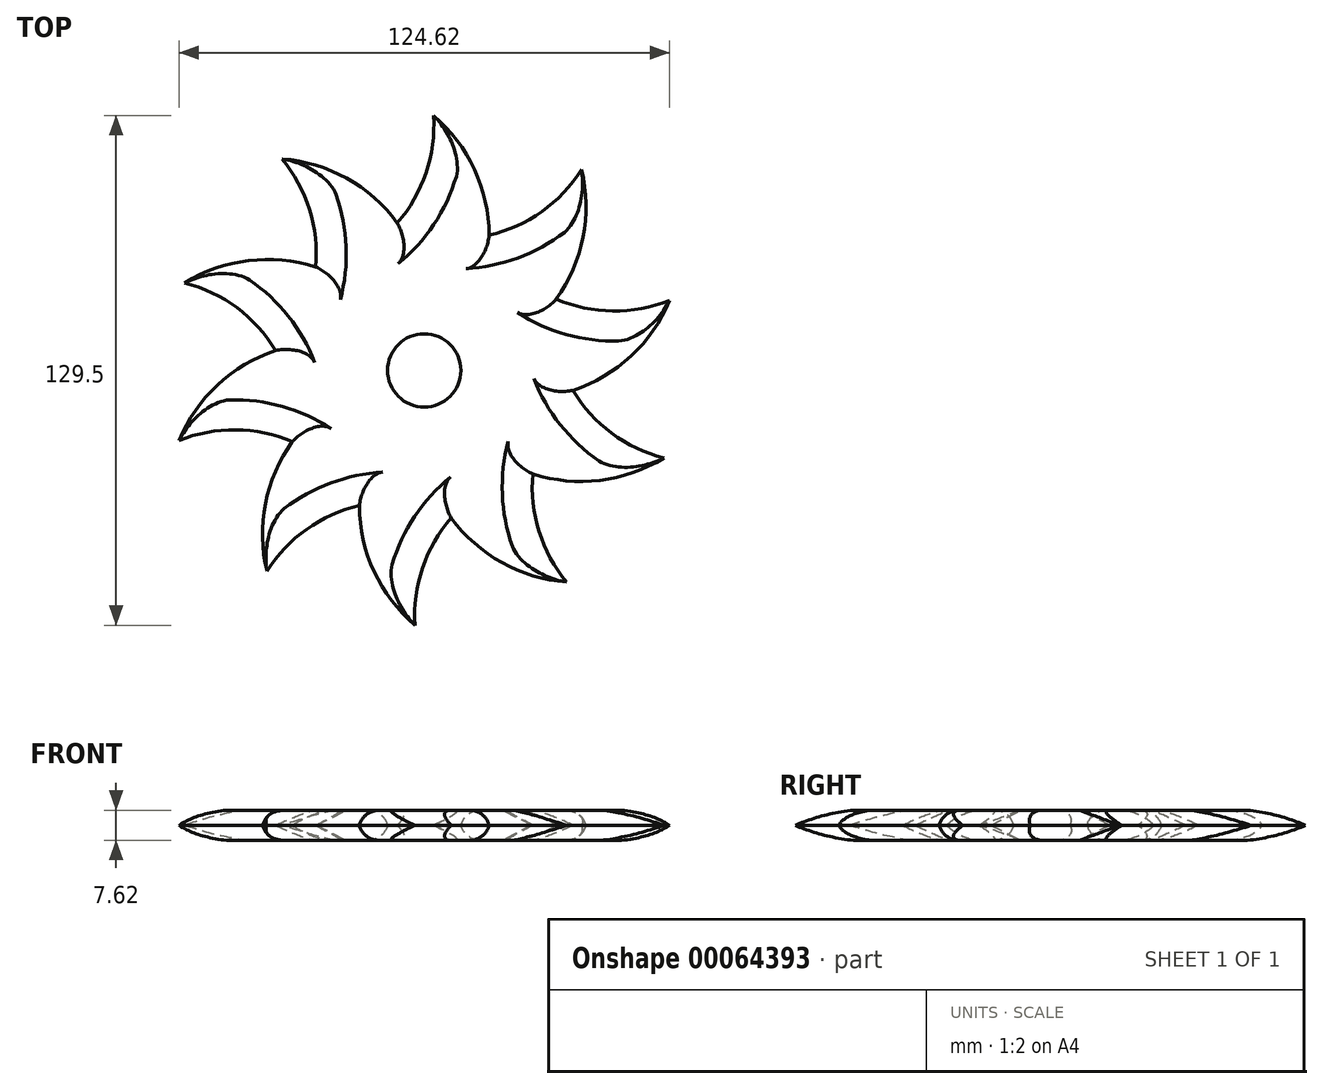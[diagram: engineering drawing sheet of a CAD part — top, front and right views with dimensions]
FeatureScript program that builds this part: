
annotation { "Feature Type Name" : "Feature", "Feature Type Description" : "" }
export const myFeature = defineFeature(function(context is Context, id is Id, definition is map)
    precondition{}
    {
        {
            var Q0;
            Q0=qCreatedBy(makeId("Top.planeOp"),FACE);
            var sketch = newSketch(context, id + "F0", { "sketchPlane" : qUnion([Q0])});
            skCircle(sketch, "E0.cCircle", {"center": v(0, 0) * mm, "radius": 38.1 * mm, "construction": true});
            skLineSegment(sketch, "E0.0", {"start": v(-27.58, 26.3) * mm, "end": v(-6.86, 37.48) * mm});
            skLineSegment(sketch, "E0.1", {"start": v(-6.86, 37.48) * mm, "end": v(16.48, 34.35) * mm});
            skLineSegment(sketch, "E0.2", {"start": v(16.48, 34.35) * mm, "end": v(33.53, 18.1) * mm});
            skLineSegment(sketch, "E0.3", {"start": v(33.53, 18.1) * mm, "end": v(37.76, -5.06) * mm});
            skLineSegment(sketch, "E0.4", {"start": v(37.76, -5.06) * mm, "end": v(27.58, -26.3) * mm});
            skLineSegment(sketch, "E0.5", {"start": v(27.58, -26.3) * mm, "end": v(6.86, -37.48) * mm});
            skLineSegment(sketch, "E0.6", {"start": v(6.86, -37.48) * mm, "end": v(-16.48, -34.35) * mm});
            skLineSegment(sketch, "E0.7", {"start": v(-16.48, -34.35) * mm, "end": v(-33.53, -18.1) * mm});
            skLineSegment(sketch, "E0.8", {"start": v(-33.53, -18.1) * mm, "end": v(-37.76, 5.06) * mm});
            skLineSegment(sketch, "E0.9", {"start": v(-37.76, 5.06) * mm, "end": v(-27.58, 26.3) * mm});
            skArc(sketch, "E1", {"start": v(-16.48, -34.35) * mm, "mid": v(-12.74, -51.1) * mm, "end": v(-2.35, -64.75) * mm});
            skArc(sketch, "E2", {"start": v(6.86, -37.48) * mm, "mid": v(-0.44, -50.2) * mm, "end": v(-2.35, -64.75) * mm});
            skArc(sketch, "E3.1.1", {"start": v(27.58, -26.3) * mm, "mid": v(29.15, -40.88) * mm, "end": v(36.16, -53.77) * mm});
            skArc(sketch, "E3.1.2", {"start": v(6.86, -37.48) * mm, "mid": v(19.73, -48.82) * mm, "end": v(36.16, -53.77) * mm});
            skArc(sketch, "E3.2.1", {"start": v(37.76, -5.06) * mm, "mid": v(47.6, -15.94) * mm, "end": v(60.85, -22.25) * mm});
            skArc(sketch, "E3.2.2", {"start": v(27.58, -26.3) * mm, "mid": v(44.66, -27.9) * mm, "end": v(60.85, -22.25) * mm});
            skArc(sketch, "E3.3.1", {"start": v(33.53, 18.1) * mm, "mid": v(47.88, 15.1) * mm, "end": v(62.3, 17.77) * mm});
            skArc(sketch, "E3.3.2", {"start": v(37.76, -5.06) * mm, "mid": v(52.53, 3.67) * mm, "end": v(62.3, 17.77) * mm});
            skArc(sketch, "E3.4.1", {"start": v(16.48, 34.35) * mm, "mid": v(29.87, 40.36) * mm, "end": v(39.96, 51) * mm});
            skArc(sketch, "E3.4.2", {"start": v(33.53, 18.1) * mm, "mid": v(40.34, 33.85) * mm, "end": v(39.96, 51) * mm});
            skArc(sketch, "E3.5.1", {"start": v(-6.86, 37.48) * mm, "mid": v(0.44, 50.2) * mm, "end": v(2.35, 64.75) * mm});
            skArc(sketch, "E3.5.2", {"start": v(16.48, 34.35) * mm, "mid": v(12.74, 51.1) * mm, "end": v(2.35, 64.75) * mm});
            skArc(sketch, "E3.6.1", {"start": v(-27.58, 26.3) * mm, "mid": v(-29.15, 40.88) * mm, "end": v(-36.16, 53.77) * mm});
            skArc(sketch, "E3.6.2", {"start": v(-6.86, 37.48) * mm, "mid": v(-19.73, 48.82) * mm, "end": v(-36.16, 53.77) * mm});
            skArc(sketch, "E3.7.1", {"start": v(-37.76, 5.06) * mm, "mid": v(-47.6, 15.94) * mm, "end": v(-60.85, 22.25) * mm});
            skArc(sketch, "E3.7.2", {"start": v(-27.58, 26.3) * mm, "mid": v(-44.66, 27.9) * mm, "end": v(-60.85, 22.25) * mm});
            skArc(sketch, "E3.8.1", {"start": v(-33.53, -18.1) * mm, "mid": v(-47.88, -15.1) * mm, "end": v(-62.3, -17.77) * mm});
            skArc(sketch, "E3.8.2", {"start": v(-37.76, 5.06) * mm, "mid": v(-52.53, -3.67) * mm, "end": v(-62.3, -17.77) * mm});
            skArc(sketch, "E3.9.1", {"start": v(-16.48, -34.35) * mm, "mid": v(-29.87, -40.36) * mm, "end": v(-39.96, -51) * mm});
            skArc(sketch, "E3.9.2", {"start": v(-33.53, -18.1) * mm, "mid": v(-40.34, -33.85) * mm, "end": v(-39.96, -51) * mm});
            skCircle(sketch, "E4", {"center": v(0, 0) * mm, "radius": 9.31 * mm});
            skSolve(sketch);
        }
        {
            var Q0;
            Q0 = qSketchRegion(id + "F0", true);
            extrude(context, id + "F1", {"entities" : qUnion([Q0]), "depth" : 3.8 * mm});
        }
        {
            var Q0;
            Q0=makeQuery(id+"F1.opExtrude","CAP_EDGE",EDGE,{"disambiguationData":[OSD([sQuery(id+"F0.wireOp",EDGE,"E2")])],"isStart":false});
            var Q1;
            Q1=makeQuery(id+"F1.opExtrude","CAP_EDGE",EDGE,{"disambiguationData":[OSD([sQuery(id+"F0.wireOp",EDGE,"E3.1.1")])],"isStart":false});
            var Q2;
            Q2=makeQuery(id+"F1.opExtrude","CAP_EDGE",EDGE,{"disambiguationData":[OSD([sQuery(id+"F0.wireOp",EDGE,"E3.2.1")])],"isStart":false});
            var Q3;
            Q3=makeQuery(id+"F1.opExtrude","CAP_EDGE",EDGE,{"disambiguationData":[OSD([sQuery(id+"F0.wireOp",EDGE,"E3.3.1")])],"isStart":false});
            var Q4;
            Q4=makeQuery(id+"F1.opExtrude","CAP_EDGE",EDGE,{"disambiguationData":[OSD([sQuery(id+"F0.wireOp",EDGE,"E3.4.1")])],"isStart":false});
            var Q5;
            Q5=makeQuery(id+"F1.opExtrude","CAP_EDGE",EDGE,{"disambiguationData":[OSD([sQuery(id+"F0.wireOp",EDGE,"E3.5.1")])],"isStart":false});
            var Q6;
            Q6=makeQuery(id+"F1.opExtrude","CAP_EDGE",EDGE,{"disambiguationData":[OSD([sQuery(id+"F0.wireOp",EDGE,"E3.6.1")])],"isStart":false});
            var Q7;
            Q7=makeQuery(id+"F1.opExtrude","CAP_EDGE",EDGE,{"disambiguationData":[OSD([sQuery(id+"F0.wireOp",EDGE,"E3.7.1")])],"isStart":false});
            var Q8;
            Q8=makeQuery(id+"F1.opExtrude","CAP_EDGE",EDGE,{"disambiguationData":[OSD([sQuery(id+"F0.wireOp",EDGE,"E3.8.1")])],"isStart":false});
            var Q9;
            Q9=makeQuery(id+"F1.opExtrude","CAP_EDGE",EDGE,{"disambiguationData":[OSD([sQuery(id+"F0.wireOp",EDGE,"E3.9.1")])],"isStart":false});
            chamfer(context, id + "F2", {"entities" : qUnion([Q0, Q1, Q2, Q3, Q4, Q5, Q6, Q7, Q8, Q9]), "chamferType" : ChamferType.TWO_OFFSETS, "width1" : 3.8 * mm, "oppositeDirection" : false, "width2" : 7.62 * mm, "tangentPropagation" : true});
        }
        {
            var Q0;
            Q0=makeQuery(id+"F1.opExtrude","CAP_EDGE",EDGE,{"disambiguationData":[OSD([sQuery(id+"F0.wireOp",EDGE,"E3.9.2")])],"isStart":false});
            var Q1;
            Q1=makeQuery(id+"F1.opExtrude","CAP_EDGE",EDGE,{"disambiguationData":[OSD([sQuery(id+"F0.wireOp",EDGE,"E3.8.2")])],"isStart":false});
            var Q2;
            Q2=makeQuery(id+"F1.opExtrude","CAP_EDGE",EDGE,{"disambiguationData":[OSD([sQuery(id+"F0.wireOp",EDGE,"E3.7.2")])],"isStart":false});
            var Q3;
            Q3=makeQuery(id+"F1.opExtrude","CAP_EDGE",EDGE,{"disambiguationData":[OSD([sQuery(id+"F0.wireOp",EDGE,"E3.6.2")])],"isStart":false});
            var Q4;
            Q4=makeQuery(id+"F1.opExtrude","CAP_EDGE",EDGE,{"disambiguationData":[OSD([sQuery(id+"F0.wireOp",EDGE,"E3.5.2")])],"isStart":false});
            var Q5;
            Q5=makeQuery(id+"F1.opExtrude","CAP_EDGE",EDGE,{"disambiguationData":[OSD([sQuery(id+"F0.wireOp",EDGE,"E3.4.2")])],"isStart":false});
            var Q6;
            Q6=makeQuery(id+"F1.opExtrude","CAP_EDGE",EDGE,{"disambiguationData":[OSD([sQuery(id+"F0.wireOp",EDGE,"E3.3.2")])],"isStart":false});
            var Q7;
            Q7=makeQuery(id+"F1.opExtrude","CAP_EDGE",EDGE,{"disambiguationData":[OSD([sQuery(id+"F0.wireOp",EDGE,"E3.2.2")])],"isStart":false});
            var Q8;
            Q8=makeQuery(id+"F1.opExtrude","CAP_EDGE",EDGE,{"disambiguationData":[OSD([sQuery(id+"F0.wireOp",EDGE,"E3.1.2")])],"isStart":false});
            var Q9;
            Q9=makeQuery(id+"F1.opExtrude","CAP_EDGE",EDGE,{"disambiguationData":[OSD([sQuery(id+"F0.wireOp",EDGE,"E1")])],"isStart":false});
            var Q10;
            Q10=makeQuery(id+"F1.opExtrude","CAP_EDGE",EDGE,{"disambiguationData":[OSD([sQuery(id+"F0.wireOp",EDGE,"E4")])],"isStart":false});
            fillet(context, id + "F3", {"entities" : qUnion([Q0, Q1, Q2, Q3, Q4, Q5, Q6, Q7, Q8, Q9, Q10]), "radius" : 5.08 * mm, "tangentPropagation" : true, "allowEdgeOverflow" : false});
        }
        {
            var Q0;
            Q0=makeQuery(id+"F1.opExtrude","SWEPT_BODY",BODY,{"disambiguationData":[OSD([sQuery(id+"F0.wireOp",EDGE,"E1"),sQuery(id+"F0.wireOp",EDGE,"E2"),sQuery(id+"F0.wireOp",EDGE,"E3.1.1"),sQuery(id+"F0.wireOp",EDGE,"E3.1.2"),sQuery(id+"F0.wireOp",EDGE,"E3.2.1"),sQuery(id+"F0.wireOp",EDGE,"E3.2.2"),sQuery(id+"F0.wireOp",EDGE,"E3.3.1"),sQuery(id+"F0.wireOp",EDGE,"E3.3.2"),sQuery(id+"F0.wireOp",EDGE,"E3.4.1"),sQuery(id+"F0.wireOp",EDGE,"E3.4.2"),sQuery(id+"F0.wireOp",EDGE,"E3.5.1"),sQuery(id+"F0.wireOp",EDGE,"E3.5.2"),sQuery(id+"F0.wireOp",EDGE,"E3.6.1"),sQuery(id+"F0.wireOp",EDGE,"E3.6.2"),sQuery(id+"F0.wireOp",EDGE,"E3.7.1"),sQuery(id+"F0.wireOp",EDGE,"E3.7.2"),sQuery(id+"F0.wireOp",EDGE,"E3.8.1"),sQuery(id+"F0.wireOp",EDGE,"E3.8.2"),sQuery(id+"F0.wireOp",EDGE,"E3.9.1"),sQuery(id+"F0.wireOp",EDGE,"E3.9.2"),sQuery(id+"F0.wireOp",EDGE,"E4")])]});
            var Q1;
            Q1=makeQuery(id+"F1.opExtrude","CAP_FACE",FACE,{"disambiguationData":[OSD([sQuery(id+"F0.wireOp",EDGE,"E1"),sQuery(id+"F0.wireOp",EDGE,"E2"),sQuery(id+"F0.wireOp",EDGE,"E3.1.1"),sQuery(id+"F0.wireOp",EDGE,"E3.1.2"),sQuery(id+"F0.wireOp",EDGE,"E3.2.1"),sQuery(id+"F0.wireOp",EDGE,"E3.2.2"),sQuery(id+"F0.wireOp",EDGE,"E3.3.1"),sQuery(id+"F0.wireOp",EDGE,"E3.3.2"),sQuery(id+"F0.wireOp",EDGE,"E3.4.1"),sQuery(id+"F0.wireOp",EDGE,"E3.4.2"),sQuery(id+"F0.wireOp",EDGE,"E3.5.1"),sQuery(id+"F0.wireOp",EDGE,"E3.5.2"),sQuery(id+"F0.wireOp",EDGE,"E3.6.1"),sQuery(id+"F0.wireOp",EDGE,"E3.6.2"),sQuery(id+"F0.wireOp",EDGE,"E3.7.1"),sQuery(id+"F0.wireOp",EDGE,"E3.7.2"),sQuery(id+"F0.wireOp",EDGE,"E3.8.1"),sQuery(id+"F0.wireOp",EDGE,"E3.8.2"),sQuery(id+"F0.wireOp",EDGE,"E3.9.1"),sQuery(id+"F0.wireOp",EDGE,"E3.9.2"),sQuery(id+"F0.wireOp",EDGE,"E4")])],"isStart":true});
            mirror(context, id + "F4", {"operationType" : NewBodyOperationType.ADD, "entities" : qUnion([Q0]), "mirrorPlane" : qUnion([Q1])});
        }
    });
